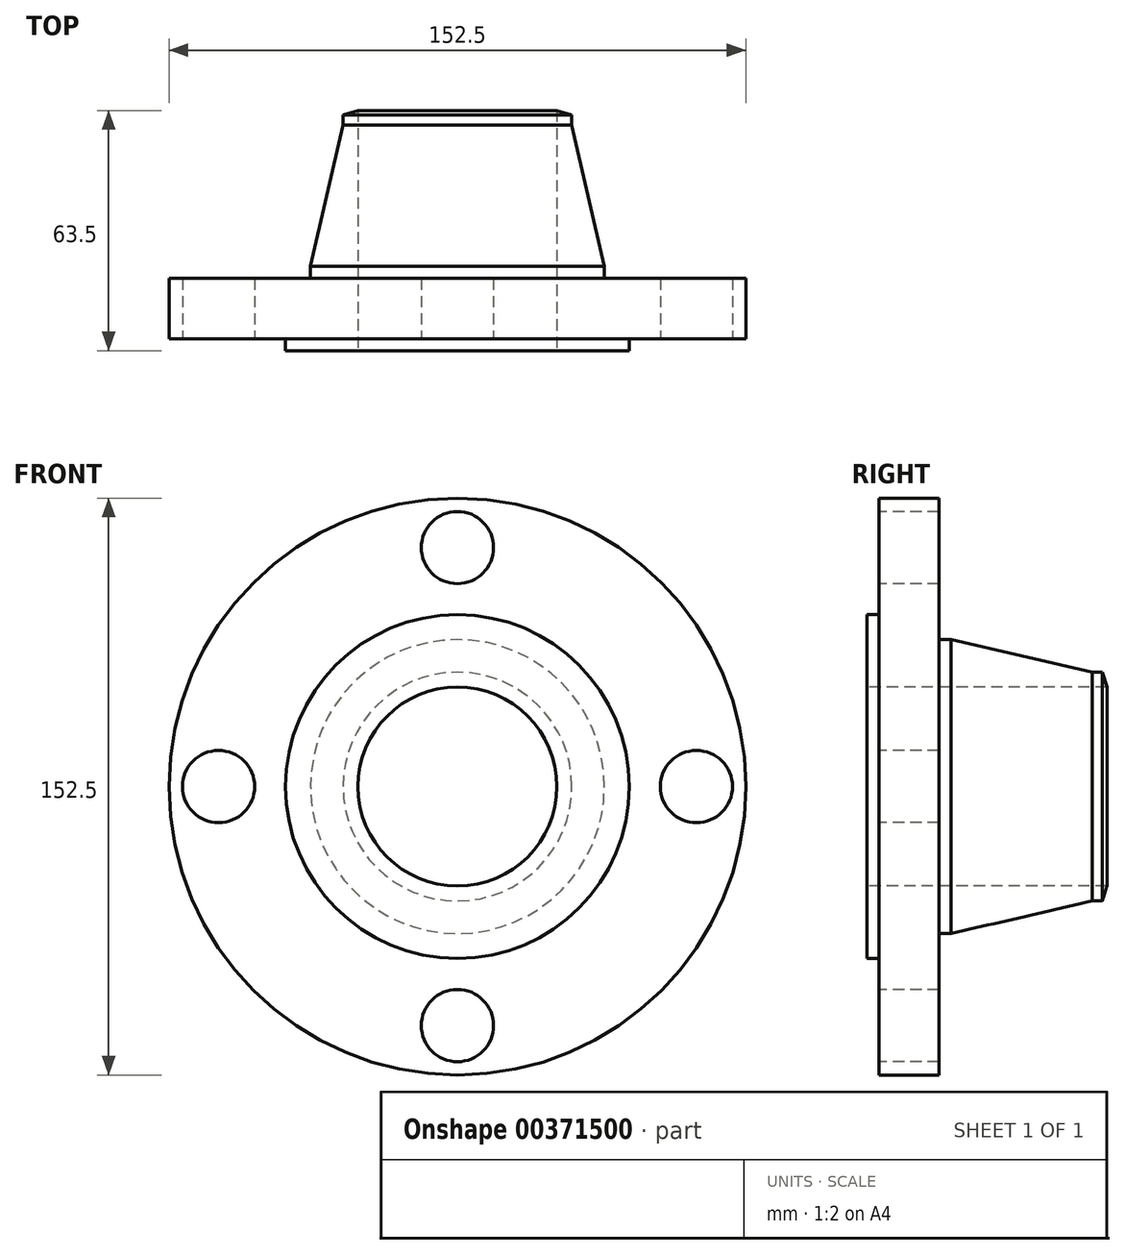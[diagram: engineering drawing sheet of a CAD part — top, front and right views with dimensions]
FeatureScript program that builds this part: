
annotation { "Feature Type Name" : "Feature", "Feature Type Description" : "" }
export const myFeature = defineFeature(function(context is Context, id is Id, definition is map)
    precondition{}
    {
        {
            var Q0;
            Q0=qCreatedBy(makeId("Right.planeOp"),FACE);
            var sketch = newSketch(context, id + "F0", { "sketchPlane" : qUnion([Q0])});
            skLineSegment(sketch, "E0", {"start": v(0, 0) * mm, "end": v(0, 19.15) * mm});
            skLineSegment(sketch, "E1", {"start": v(0, 19.15) * mm, "end": v(3.17, 19.15) * mm});
            skLineSegment(sketch, "E2", {"start": v(3.17, 19.15) * mm, "end": v(3.17, 49.95) * mm});
            skLineSegment(sketch, "E3", {"start": v(3.17, 49.95) * mm, "end": v(19.1, 49.95) * mm});
            skLineSegment(sketch, "E4", {"start": v(19.1, 49.95) * mm, "end": v(19.1, 12.55) * mm});
            skLineSegment(sketch, "E5", {"start": v(19.1, 12.55) * mm, "end": v(22.27, 12.55) * mm});
            skLineSegment(sketch, "E6", {"start": v(59.64, 3.95) * mm, "end": v(22.27, 12.55) * mm});
            skLineSegment(sketch, "E7", {"start": v(59.64, 3.95) * mm, "end": v(62.3, 3.95) * mm});
            skLineSegment(sketch, "E8", {"start": v(62.3, 3.95) * mm, "end": v(63.5, 0) * mm});
            skLineSegment(sketch, "E9", {"start": v(63.5, 0) * mm, "end": v(0, 0) * mm});
            skLineSegment(sketch, "E10", {"start": v(-65.53, -26.3) * mm, "end": v(75.52, -26.3) * mm, "construction": true});
            skSolve(sketch);
        }
        {
            var Q0;
            Q0=makeQuery(id+"F0.imprint","IMPRINT",FACE,{"disambiguationData":[TD([[makeQuery(id+"F0.imprint","IMPRINT",EDGE,{"derivedFrom":sQuery(id+"F0.wireOp",EDGE,"E0")}),-1.0]])]});
            var Q1;
            Q1=sQuery(id+"F0.wireOp",EDGE,"E10");
            revolve(context, id + "F1", {"entities" : qUnion([Q0]), "axis" : qUnion([Q1]), "revolveType" : RevolveType.FULL});
        }
        {
            var Q0;
            Q0=makeQuery(id+"F1.opRevolve","SWEPT_FACE",FACE,{"disambiguationData":[OSD([sQuery(id+"F0.wireOp",EDGE,"E2")])]});
            var sketch = newSketch(context, id + "F2", { "sketchPlane" : qUnion([Q0])});
            skLineSegment(sketch, "E11", {"start": v(0, -26.3) * mm, "end": v(0, 36.89) * mm, "construction": true});
            skCircle(sketch, "E12", {"center": v(0, 36.89) * mm, "radius": 9.55 * mm});
            skCircle(sketch, "E13.1.0", {"center": v(-63.19, -26.3) * mm, "radius": 9.55 * mm});
            skCircle(sketch, "E13.2.0", {"center": v(0, -89.48) * mm, "radius": 9.55 * mm});
            skCircle(sketch, "E13.3.0", {"center": v(63.19, -26.3) * mm, "radius": 9.55 * mm});
            skPoint(sketch, "E13.center", {"position": v(0, -26.3) * mm});
            skSolve(sketch);
        }
        {
            var Q0;
            Q0=makeQuery(id+"F2.imprint","IMPRINT",FACE,{"disambiguationData":[TD([[makeQuery(id+"F2.imprint","IMPRINT",EDGE,{"derivedFrom":sQuery(id+"F2.wireOp",EDGE,"E12")}),1.0]])]});
            var Q1;
            Q1=makeQuery(id+"F2.imprint","IMPRINT",FACE,{"disambiguationData":[TD([[makeQuery(id+"F2.imprint","IMPRINT",EDGE,{"derivedFrom":sQuery(id+"F2.wireOp",EDGE,"E13.3.0")}),1.0]])]});
            var Q2;
            Q2=makeQuery(id+"F2.imprint","IMPRINT",FACE,{"disambiguationData":[TD([[makeQuery(id+"F2.imprint","IMPRINT",EDGE,{"derivedFrom":sQuery(id+"F2.wireOp",EDGE,"E13.2.0")}),1.0]])]});
            var Q3;
            Q3=makeQuery(id+"F2.imprint","IMPRINT",FACE,{"disambiguationData":[TD([[makeQuery(id+"F2.imprint","IMPRINT",EDGE,{"derivedFrom":sQuery(id+"F2.wireOp",EDGE,"E13.1.0")}),1.0]])]});
            extrude(context, id + "F3", {"entities" : qUnion([Q0, Q1, Q2, Q3]), "operationType" : NewBodyOperationType.REMOVE, "endBound" : BoundingType.THROUGH_ALL, "oppositeDirection" : true, "depth" : 25.4 * mm});
        }
    });
